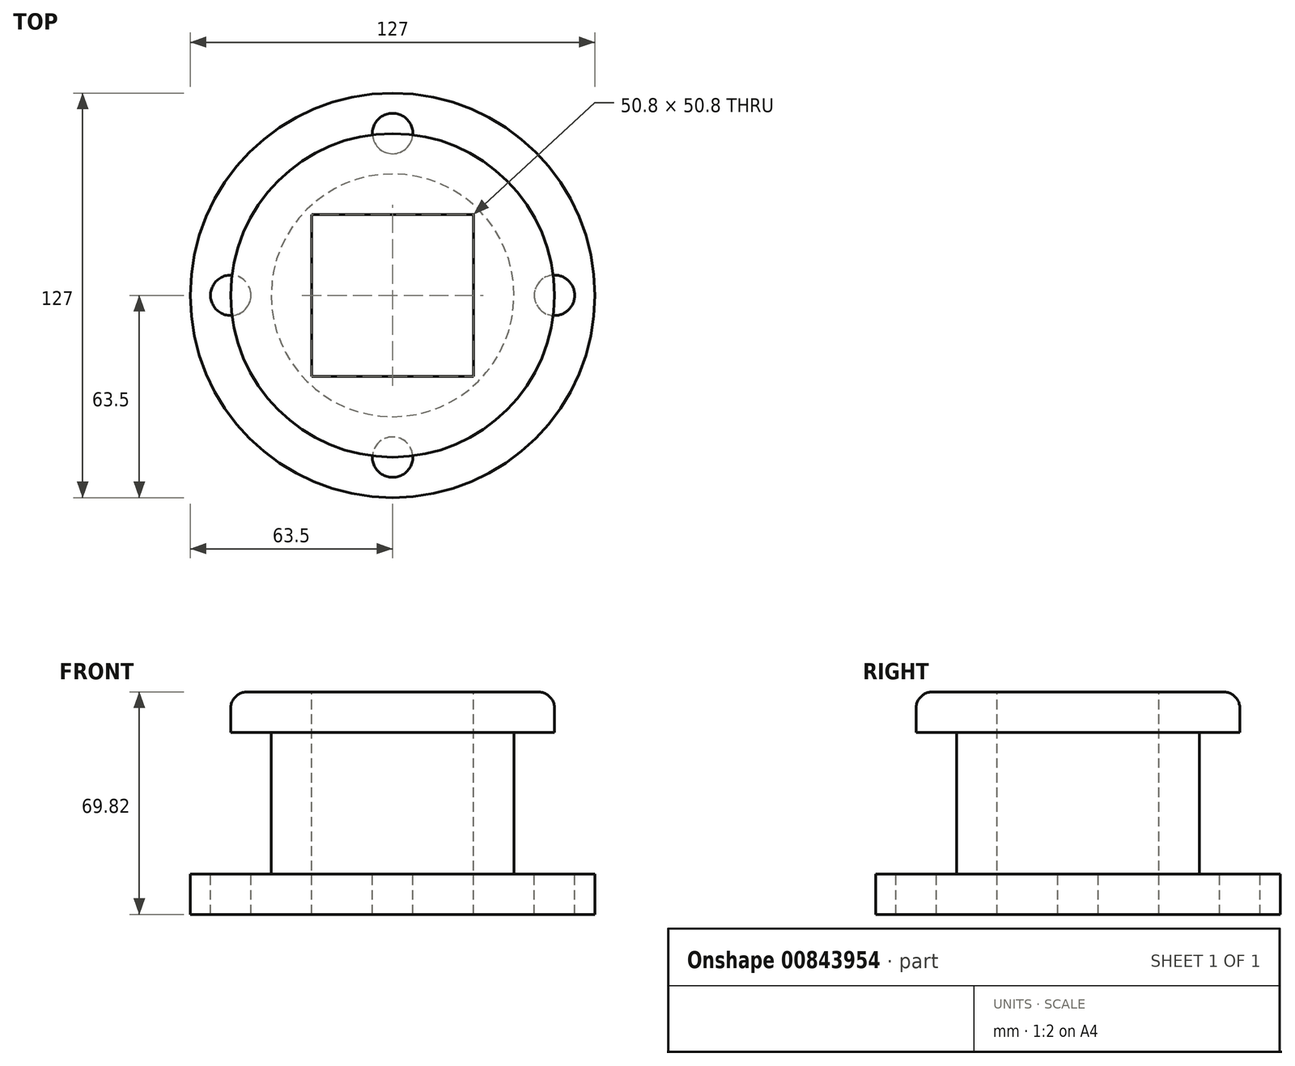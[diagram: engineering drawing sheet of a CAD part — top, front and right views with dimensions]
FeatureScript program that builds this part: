
annotation { "Feature Type Name" : "Feature", "Feature Type Description" : "" }
export const myFeature = defineFeature(function(context is Context, id is Id, definition is map)
    precondition{}
    {
        {
            var Q0;
            Q0=qCreatedBy(makeId("Top.planeOp"),FACE);
            var sketch = newSketch(context, id + "F0", { "sketchPlane" : qUnion([Q0])});
            skCircle(sketch, "E0", {"center": v(0, 0) * mm, "radius": 63.5 * mm});
            skSolve(sketch);
        }
        {
            var Q0;
            Q0 = qSketchRegion(id + "F0", true);
            extrude(context, id + "F1", {"entities" : qUnion([Q0]), "depth" : 12.7 * mm, "offsetDistance" : 25.4 * mm});
        }
        {
            var Q0;
            Q0=qCreatedBy(makeId("Top.planeOp"),FACE);
            var sketch = newSketch(context, id + "F2", { "sketchPlane" : qUnion([Q0])});
            skCircle(sketch, "E1", {"center": v(0, 0) * mm, "radius": 38.1 * mm});
            skSolve(sketch);
        }
        {
            var Q0;
            Q0 = qSketchRegion(id + "F2", true);
            extrude(context, id + "F3", {"entities" : qUnion([Q0]), "operationType" : NewBodyOperationType.ADD, "depth" : 57.15 * mm, "offsetDistance" : 25.4 * mm});
        }
        {
            var Q0;
            Q0=makeQuery(id+"F1.opExtrude","SWEPT_BODY",BODY,{"disambiguationData":[OSD([sQuery(id+"F0.wireOp",EDGE,"E0")])]});
            transform(context, id + "F4", {"entities" : qUnion([Q0]), "transformType" : TransformType.TRANSLATION_3D, "dx" : 0 * mm, "dy" : 0 * mm, "dz" : -57.12 * mm, "makeCopy" : false});
        }
        {
            var Q0;
            Q0=qCreatedBy(makeId("Top.planeOp"),FACE);
            var sketch = newSketch(context, id + "F5", { "sketchPlane" : qUnion([Q0])});
            skCircle(sketch, "E2", {"center": v(0, 0) * mm, "radius": 50.8 * mm});
            skSolve(sketch);
        }
        {
            var Q0;
            Q0 = qSketchRegion(id + "F5", true);
            extrude(context, id + "F6", {"entities" : qUnion([Q0]), "operationType" : NewBodyOperationType.ADD, "depth" : 12.7 * mm, "offsetDistance" : 25.4 * mm});
        }
        {
            var Q0;
            Q0=makeQuery(id+"F1.opExtrude","SWEPT_BODY",BODY,{"disambiguationData":[OSD([sQuery(id+"F0.wireOp",EDGE,"E0")])]});
            transform(context, id + "F7", {"entities" : qUnion([Q0]), "transformType" : TransformType.TRANSLATION_3D, "dx" : 0 * mm, "dy" : 0 * mm, "dz" : -12.7 * mm, "makeCopy" : false});
        }
        {
            var Q0;
            Q0=qCreatedBy(makeId("Top.planeOp"),FACE);
            var sketch = newSketch(context, id + "F8", { "sketchPlane" : qUnion([Q0])});
            skLineSegment(sketch, "E3.bottom", {"start": v(25.4, -25.4) * mm, "end": v(-25.4, -25.4) * mm});
            skLineSegment(sketch, "E3.top", {"start": v(25.4, 25.4) * mm, "end": v(-25.4, 25.4) * mm});
            skLineSegment(sketch, "E3.left", {"start": v(25.4, -25.4) * mm, "end": v(25.4, 25.4) * mm});
            skLineSegment(sketch, "E3.right", {"start": v(-25.4, -25.4) * mm, "end": v(-25.4, 25.4) * mm});
            skPoint(sketch, "E3.middle", {"position": v(0, 0) * mm});
            skSolve(sketch);
        }
        {
            var Q0;
            Q0 = qSketchRegion(id + "F8", true);
            extrude(context, id + "F9", {"entities" : qUnion([Q0]), "operationType" : NewBodyOperationType.REMOVE, "oppositeDirection" : true, "depth" : 82.55 * mm, "offsetDistance" : 25.4 * mm});
        }
        {
            var Q0;
            Q0=makeQuery(id+"F6.opExtrude","CAP_EDGE",EDGE,{"disambiguationData":[OSD([sQuery(id+"F5.wireOp",EDGE,"E2")])],"isStart":false});
            fillet(context, id + "F10", {"entities" : qUnion([Q0]), "radius" : 5.08 * mm, "tangentPropagation" : true, "allowEdgeOverflow" : false});
        }
        {
            var Q0;
            Q0=makeQuery(id+"F1.opExtrude","SWEPT_BODY",BODY,{"disambiguationData":[OSD([sQuery(id+"F0.wireOp",EDGE,"E0")])]});
            transform(context, id + "F11", {"entities" : qUnion([Q0]), "transformType" : TransformType.TRANSLATION_3D, "dx" : 0 * mm, "dy" : 0 * mm, "dz" : 57.12 * mm, "makeCopy" : false});
        }
        {
            var Q0;
            Q0=qCreatedBy(makeId("Top.planeOp"),FACE);
            var sketch = newSketch(context, id + "F12", { "sketchPlane" : qUnion([Q0])});
            skCircle(sketch, "E4", {"center": v(0, -50.8) * mm, "radius": 6.35 * mm});
            skCircle(sketch, "E5.1.0", {"center": v(50.8, 0) * mm, "radius": 6.35 * mm});
            skCircle(sketch, "E5.2.0", {"center": v(0, 50.8) * mm, "radius": 6.35 * mm});
            skCircle(sketch, "E5.3.0", {"center": v(-50.8, 0) * mm, "radius": 6.35 * mm});
            skPoint(sketch, "E5.center", {"position": v(0, 0) * mm});
            skSolve(sketch);
        }
        {
            var Q0;
            Q0 = qSketchRegion(id + "F12", true);
            extrude(context, id + "F13", {"entities" : qUnion([Q0]), "operationType" : NewBodyOperationType.REMOVE, "oppositeDirection" : true, "depth" : 25.4 * mm, "offsetDistance" : 25.4 * mm});
        }
    });
